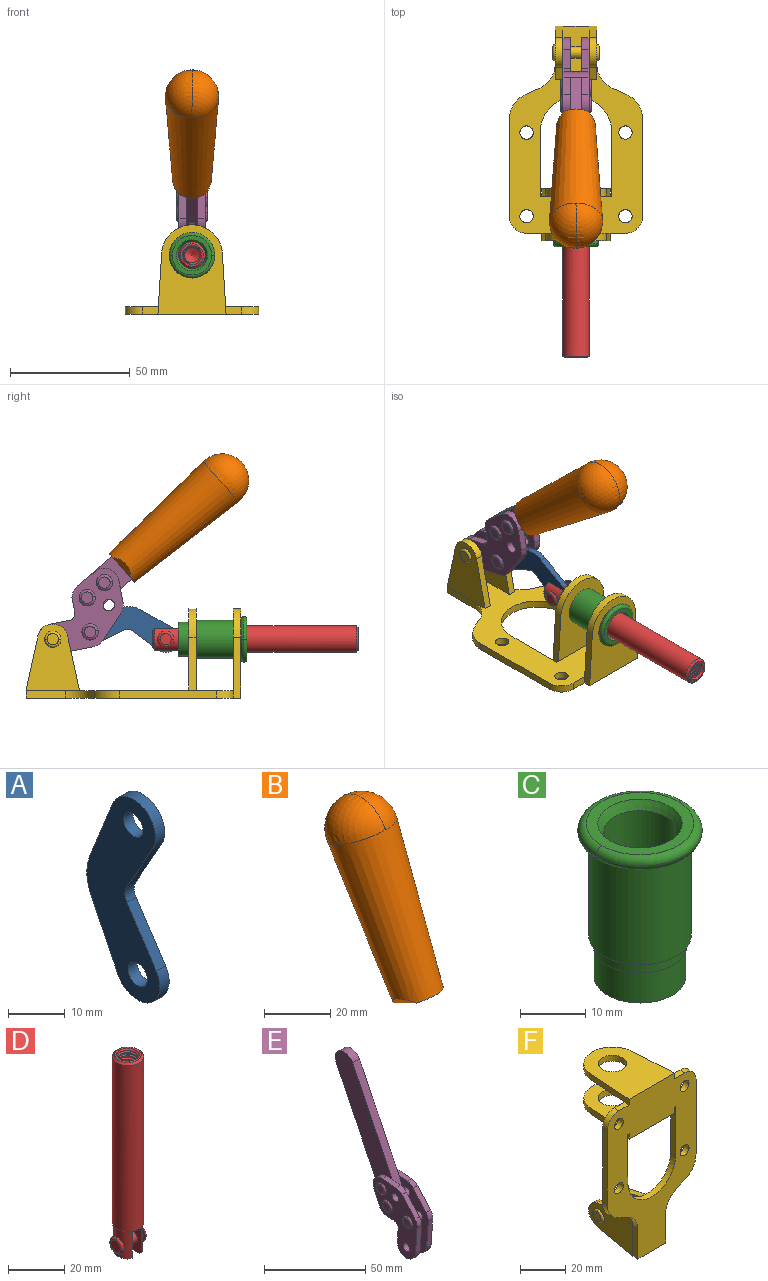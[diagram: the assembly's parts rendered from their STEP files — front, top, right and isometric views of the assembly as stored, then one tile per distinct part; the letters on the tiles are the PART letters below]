
ASSEMBLY  parts=6 mates=6
PART A: 12 faces, bbox 2.3x18.2x42.8 mm
  f0: cylinder r=2.4mm len=4.8mm, axis (1,0,0), area 34.9mm2, adj f4,f11
  f1: cylinder r=10.41mm len=8.47mm, axis (1,0,0), area 20.2mm2, adj f4,f9,f10,f11
  f2: cylinder r=3.05mm len=3.16mm, axis (1,0,0), area 7.7mm2, adj f4,f6,f7,f11
  f3: cylinder r=2.4mm len=4.8mm, axis (1,0,0), area 34.9mm2, adj f4,f11
  f4: plane 42.81x18.23mm, normal (-1,0,0), area 414.1mm2, adj f0,f1,f2,f3,f5,f6,f7,f8
  f5: cylinder r=5.54mm len=10.67mm, axis (1,0,0), area 41.8mm2, adj f4,f6,f10,f11
  f6: plane 11.66x6.53mm, normal (0,-0.87,-0.49), area 30.9mm2, adj f2,f4,f5,f11
  f7: plane 11.17x7.33mm, normal (0,-0.84,0.55), area 30.9mm2, adj f2,f4,f8,f11
  f8: cylinder r=5.54mm len=10.51mm, axis (1,0,0), area 41.8mm2, adj f4,f7,f9,f11
  f9: plane 13.67x6.67mm, normal (0,0.9,-0.44), area 35.1mm2, adj f1,f4,f8,f11
  f10: plane 14.1x5.7mm, normal (0,0.93,0.37), area 35.1mm2, adj f1,f4,f5,f11
  f11: plane 42.81x18.23mm, normal (1,0,0), area 414.1mm2, adj f0,f1,f2,f3,f5,f6,f7,f8
PART B: 11 faces, bbox 22.3x42.6x64.5 mm
  f0: sphere r=11.13mm, area 411.4mm2, adj f1,f8
  f1: cone r=11.11mm half-angle=3.3deg, axis (0,0.44,0.9), area 3251.8mm2, adj f0,f7,f8,f9,f10
  f2: cylinder r=6.16mm len=11.7mm, axis (1,0,0), area 89.5mm2, adj f3,f4,f5,f6
  f3: plane 60.23x36.75mm, normal (-1,0,0), area 763.6mm2, adj f2,f4,f6,f10
  f4: plane 51.37x25.05mm, normal (0,0.9,-0.44), area 264.2mm2, adj f2,f3,f5,f10
  f5: plane 60.23x36.75mm, normal (1,0,0), area 763.6mm2, adj f2,f4,f6,f10
  f6: plane 51.37x25.05mm, normal (0,-0.9,0.44), area 264.2mm2, adj f2,f3,f5,f10
  f7: plane 9.95x5.95mm, normal (0.71,-0.31,-0.64), area 25.8mm2, adj f1,f10
  f8: sphere r=11.13mm, area 411.4mm2, adj f0,f1
  f9: plane 9.95x5.95mm, normal (-0.71,-0.31,-0.64), area 25.8mm2, adj f1,f10
  f10: plane 14.27x11.38mm, normal (0,-0.44,-0.9), area 106.7mm2, adj f1,f3,f4,f5,f6,f7,f9
PART C: 15 faces, bbox 20.6x20.6x28.7 mm
  f0: torus R=8.26mm, axis (0,0,1), area 56.8mm2, adj f1,f10,f12
  f1: torus R=8.26mm, axis (0,0,1), area 56.8mm2, adj f0,f6,f13
  f2: cylinder r=5.59mm len=25.91mm, axis (0,0,1), area 909.6mm2, adj f3,f4
  f3: cone r=6.86mm half-angle=45deg, axis (0,0,-1), area 70.2mm2, adj f2,f14
  f4: cone r=6.47mm half-angle=30deg, axis (0,0,1), area 66.7mm2, adj f2,f13
  f5: cylinder r=7.04mm len=14.07mm, axis (0,0,1), area 252.6mm2, adj f11,f14
  f6: torus R=8.26mm, axis (0,0,1), area 56.8mm2, adj f1,f12,f13
  f7: cylinder r=7.16mm len=14.33mm, axis (0,0,1), area 91.5mm2, adj f9,f11
  f8: cylinder r=7.86mm len=18.42mm, axis (0,0,1), area 909.6mm2, adj f9,f10
  f9: plane 15.72x15.72mm, normal (0,0,-1), area 33mm2, adj f7,f8
  f10: plane 16.51x16.51mm, normal (0,0,-1), area 19.9mm2, adj f0,f8,f12
  f11: plane 14.33x14.33mm, normal (0,0,-1), area 5.7mm2, adj f5,f7
  f12: torus R=8.26mm, axis (0,0,1), area 56.8mm2, adj f0,f6,f10
  f13: plane 16.51x16.51mm, normal (0,0,1), area 82.7mm2, adj f1,f4,f6
  f14: plane 14.07x14.07mm, normal (0,0,-1), area 7.8mm2, adj f3,f5
PART D: 48 faces, bbox 12.6x11.1x86.1 mm
  f0: torus R=2.41mm, axis (-1,0,0), area 15mm2, adj f30,f32,f34
  f1: torus R=2.41mm, axis (-1,0,0), area 15mm2, adj f29,f31,f33
  f2: cylinder r=5.54mm len=72.39mm, axis (0,0,1), area 2518.5mm2, adj f3,f4,f42,f43
  f3: cone r=5.54mm half-angle=45deg, axis (0,0,1), area 7.6mm2, adj f2,f5,f41
  f4: cone r=5.54mm half-angle=45deg, axis (0,0,-1), area 34.9mm2, adj f2,f39
  f5: cylinder r=5.08mm len=11.48mm, axis (0,0,1), area 108.3mm2, adj f3,f7,f8,f41
  f6: cylinder r=2.41mm len=4.83mm, axis (-1,0,0), area 71.2mm2, adj f40,f41
  f7: cylinder r=2.41mm len=4.83mm, axis (-1,0,0), area 7.6mm2, adj f5,f34
  f8: cone r=5.08mm half-angle=45deg, axis (0,0,1), area 10.6mm2, adj f5,f37,f41
  f9: cone r=3.98mm half-angle=45deg, axis (0,0,1), area 17.6mm2, adj f27,f39,f45,f46,f47
  f10: cylinder r=2.41mm len=4.83mm, axis (-1,0,0), area 7.6mm2, adj f33,f38
  f11: cylinder r=3.2mm len=6.4mm, axis (0,0,1), area 78.4mm2, adj f12,f28,f44,f45,f47
  f12: cylinder r=3.2mm len=6.4mm, axis (0,0,1), area 10.5mm2, adj f11,f13,f45,f47
  f13: cylinder r=3.2mm len=6.4mm, axis (0,0,1), area 10.5mm2, adj f12,f14,f45,f47
  f14: cylinder r=3.2mm len=6.4mm, axis (0,0,1), area 10.5mm2, adj f13,f15,f45,f47
  f15: cylinder r=3.2mm len=6.4mm, axis (0,0,1), area 10.5mm2, adj f14,f16,f45,f47
  f16: cylinder r=3.2mm len=6.4mm, axis (0,0,1), area 10.5mm2, adj f15,f17,f45,f47
  f17: cylinder r=3.2mm len=6.4mm, axis (0,0,1), area 10.5mm2, adj f16,f18,f45,f47
  f18: cylinder r=3.2mm len=6.4mm, axis (0,0,1), area 10.5mm2, adj f17,f19,f45,f47
  f19: cylinder r=3.2mm len=6.4mm, axis (0,0,1), area 10.5mm2, adj f18,f20,f45,f47
  f20: cylinder r=3.2mm len=6.4mm, axis (0,0,1), area 10.5mm2, adj f19,f21,f45,f47
  f21: cylinder r=3.2mm len=6.4mm, axis (0,0,1), area 10.5mm2, adj f20,f22,f45,f47
  f22: cylinder r=3.2mm len=6.4mm, axis (0,0,1), area 10.5mm2, adj f21,f23,f45,f47
  f23: cylinder r=3.2mm len=6.4mm, axis (0,0,1), area 10.5mm2, adj f22,f24,f45,f47
  f24: cylinder r=3.2mm len=6.4mm, axis (0,0,1), area 10.5mm2, adj f23,f25,f45,f47
  f25: cylinder r=3.2mm len=6.4mm, axis (0,0,1), area 10.5mm2, adj f24,f26,f45,f47
  f26: cylinder r=3.2mm len=6.4mm, axis (0,0,1), area 10.5mm2, adj f25,f27,f45,f47
  f27: cylinder r=3.2mm len=6.4mm, axis (0,0,1), area 7.4mm2, adj f9,f26,f45,f47
  f28: cone r=3.2mm half-angle=60deg, axis (0,0,1), area 37.2mm2, adj f11
  f29: plane 4.83x4.83mm, normal (-1,0,0), area 18.3mm2, adj f1,f31
  f30: plane 4.83x4.83mm, normal (1,0,0), area 18.3mm2, adj f0,f32
  f31: torus R=2.41mm, axis (-1,0,0), area 15mm2, adj f1,f29,f33
  f32: torus R=2.41mm, axis (-1,0,0), area 15mm2, adj f0,f30,f34
  f33: plane 6.83x6.83mm, normal (1,0,0), area 18.3mm2, adj f1,f10,f31
  f34: plane 6.83x6.83mm, normal (-1,0,0), area 18.3mm2, adj f0,f7,f32
  f35: cone r=5.08mm half-angle=45deg, axis (0,0,1), area 10.6mm2, adj f36,f38,f40
  f36: plane 7.25x1.97mm, normal (0,0,-1), area 10mm2, adj f35,f40
  f37: plane 7.25x1.97mm, normal (0,0,-1), area 10mm2, adj f8,f41
  f38: cylinder r=5.08mm len=11.48mm, axis (0,0,1), area 108.3mm2, adj f10,f35,f40,f42
  f39: plane 9.55x9.55mm, normal (0,0,1), area 22mm2, adj f4,f9
  f40: plane 12.76x10.09mm, normal (1,0,0), area 95.7mm2, adj f6,f35,f36,f38,f42,f43
  f41: plane 12.76x10.09mm, normal (-1,0,0), area 95.7mm2, adj f3,f5,f6,f8,f37,f43
  f42: cone r=5.54mm half-angle=45deg, axis (0,0,1), area 7.6mm2, adj f2,f38,f40
  f43: plane 11.07x4.7mm, normal (0,0,-1), area 50.4mm2, adj f2,f40,f41
  f44: plane 0.89x0.62mm, normal (-1,0,0), area 0.3mm2, adj f11,f45,f46,f47
  f45: bspline ~24.8x7.63mm, area 266.6mm2, adj f9,f11,f12,f13,f14,f15,f16,f17
  f46: bspline ~24.87x7.63mm, area 73.6mm2, adj f9,f44,f45,f47
  f47: bspline ~24.98x7.63mm, area 272.5mm2, adj f9,f11,f12,f13,f14,f15,f16,f17
PART E: 59 faces, bbox 12.9x60.2x99.6 mm
  f0: torus R=2.39mm, axis (-1,0,0), area 14.9mm2, adj f20,f43,f51
  f1: torus R=2.39mm, axis (-1,0,0), area 14.9mm2, adj f19,f42,f51
  f2: torus R=2.39mm, axis (-1,0,0), area 14.9mm2, adj f18,f35,f51
  f3: torus R=2.39mm, axis (-1,0,0), area 14.9mm2, adj f14,f17,f23
  f4: torus R=2.39mm, axis (-1,0,0), area 14.9mm2, adj f13,f16,f23
  f5: torus R=2.39mm, axis (-1,0,0), area 14.9mm2, adj f12,f15,f23
  f6: cylinder r=2.39mm len=4.78mm, axis (1,0,0), area 46.5mm2, adj f48,f50,f51
  f7: cylinder r=2.39mm len=4.78mm, axis (1,0,0), area 46.5mm2, adj f50,f51
  f8: cylinder r=6.35mm len=12.68mm, axis (1,0,0), area 61.8mm2, adj f38,f39,f50,f51
  f9: cylinder r=2.39mm len=4.78mm, axis (-1,0,0), area 70.5mm2, adj f46,f50
  f10: cylinder r=2.39mm len=4.78mm, axis (-1,0,0), area 46.5mm2, adj f23,f45,f46
  f11: cylinder r=2.39mm len=4.78mm, axis (-1,0,0), area 46.5mm2, adj f23,f46
  f12: plane 4.78x4.78mm, normal (1,0,0), area 17.9mm2, adj f5,f15
  f13: plane 4.78x4.78mm, normal (1,0,0), area 17.9mm2, adj f4,f16
  f14: plane 4.78x4.78mm, normal (1,0,0), area 17.9mm2, adj f3,f17
  f15: torus R=2.39mm, axis (-1,0,0), area 14.9mm2, adj f5,f12,f23
  f16: torus R=2.39mm, axis (-1,0,0), area 14.9mm2, adj f4,f13,f23
  f17: torus R=2.39mm, axis (-1,0,0), area 14.9mm2, adj f3,f14,f23
  f18: plane 4.78x4.78mm, normal (-1,0,0), area 17.9mm2, adj f2,f35
  f19: plane 4.78x4.78mm, normal (-1,0,0), area 17.9mm2, adj f1,f42
  f20: plane 4.78x4.78mm, normal (-1,0,0), area 17.9mm2, adj f0,f43
  f21: plane 2.26x0.2mm, normal (1,0,0), area 0.2mm2, adj f31,f44
  f22: plane 2.26x0.2mm, normal (-1,0,0), area 0.2mm2, adj f41,f44
  f23: plane 39.37x30.77mm, normal (1,0,0), area 565.5mm2, adj f3,f4,f5,f10,f11,f15,f16,f17
  f24: cylinder r=6.1mm len=4.15mm, axis (-1,0,0), area 14.7mm2, adj f23,f25,f32,f46
  f25: plane 10.25x9.01mm, normal (0,-0.75,0.66), area 42.3mm2, adj f23,f24,f26,f46
  f26: cylinder r=6.35mm len=4.64mm, axis (-1,0,0), area 15.6mm2, adj f23,f25,f27,f46
  f27: plane 15.84x3.1mm, normal (0,-1,-0.07), area 49.2mm2, adj f23,f26,f28,f46
  f28: cylinder r=6.35mm len=12.68mm, axis (-1,0,0), area 61.8mm2, adj f23,f27,f29,f46
  f29: plane 8.11x3.1mm, normal (0,1,0.07), area 25.2mm2, adj f23,f28,f30,f46
  f30: cylinder r=3.05mm len=3.25mm, axis (-1,0,0), area 14.8mm2, adj f23,f29,f31,f46
  f31: plane 5.99x3.1mm, normal (0,0.07,-1), area 18.6mm2, adj f21,f23,f30,f44,f46
  f32: plane 9.5x3.1mm, normal (0,-0.07,1), area 29.5mm2, adj f23,f24,f33,f46,f47
  f33: cylinder r=6.1mm len=8.63mm, axis (-1,0,0), area 39.1mm2, adj f23,f32,f34,f47
  f34: plane 8.65x3.96mm, normal (0,0.91,-0.42), area 29.5mm2, adj f23,f33,f44,f47
  f35: torus R=2.39mm, axis (-1,0,0), area 14.9mm2, adj f2,f18,f51
  f36: plane 10.25x9.01mm, normal (0,-0.75,0.66), area 42.3mm2, adj f37,f49,f50,f51
  f37: cylinder r=6.35mm len=4.64mm, axis (1,0,0), area 15.6mm2, adj f36,f38,f50,f51
  f38: plane 15.84x3.1mm, normal (0,-1,-0.07), area 49.2mm2, adj f8,f37,f50,f51
  f39: plane 8.11x3.1mm, normal (0,1,0.07), area 25.2mm2, adj f8,f40,f50,f51
  f40: cylinder r=3.05mm len=3.25mm, axis (1,0,0), area 14.8mm2, adj f39,f41,f50,f51
  f41: plane 5.99x3.1mm, normal (0,0.07,-1), area 18.6mm2, adj f22,f40,f44,f50,f51
  f42: torus R=2.39mm, axis (-1,0,0), area 14.9mm2, adj f1,f19,f51
  f43: torus R=2.39mm, axis (-1,0,0), area 14.9mm2, adj f0,f20,f51
  f44: cylinder r=6.35mm len=12.12mm, axis (-1,0,0), area 128.9mm2, adj f21,f22,f23,f31,f34,f41,f46,f47
  f45: plane 2.65x1.35mm, normal (1,0,0), area 1mm2, adj f10,f55
  f46: plane 39.08x20.42mm, normal (-1,0,0), area 412.5mm2, adj f9,f10,f11,f24,f25,f26,f27,f28
  f47: plane 77.62x39.82mm, normal (1,0,0), area 850mm2, adj f32,f33,f34,f44,f53,f54,f55
  f48: plane 2.65x1.35mm, normal (-1,0,0), area 1mm2, adj f6,f55
  f49: cylinder r=6.1mm len=4.15mm, axis (1,0,0), area 14.7mm2, adj f36,f50,f51,f56
  f50: plane 39.08x20.42mm, normal (1,0,0), area 412.5mm2, adj f6,f7,f8,f9,f36,f37,f38,f39
  f51: plane 39.37x30.77mm, normal (-1,0,0), area 565.5mm2, adj f0,f1,f2,f6,f7,f8,f35,f36
  f52: plane 8.65x3.96mm, normal (0,0.91,-0.42), area 29.5mm2, adj f44,f51,f57,f58
  f53: plane 68.49x33.4mm, normal (0,0.9,-0.44), area 358.1mm2, adj f44,f47,f54,f58
  f54: cylinder r=6.35mm len=12.06mm, axis (1,0,0), area 93.7mm2, adj f47,f53,f55,f58
  f55: plane 68.49x33.4mm, normal (0,-0.9,0.44), area 358.1mm2, adj f44,f45,f46,f47,f48,f50,f54,f58
  f56: plane 9.5x3.1mm, normal (0,-0.07,1), area 29.5mm2, adj f49,f50,f51,f57,f58
  f57: cylinder r=6.1mm len=8.63mm, axis (1,0,0), area 39.1mm2, adj f51,f52,f56,f58
  f58: plane 77.62x39.82mm, normal (-1,0,0), area 850mm2, adj f44,f52,f53,f54,f55,f56,f57
PART F: 55 faces, bbox 55.7x37.4x89.8 mm
  f0: torus R=2.41mm, axis (-1,0,0), area 15mm2, adj f11,f15,f25
  f1: torus R=2.41mm, axis (-1,0,0), area 15mm2, adj f10,f12,f22
  f2: cylinder r=2.78mm len=5.56mm, axis (0,-1,0), area 54.2mm2, adj f30,f54
  f3: cylinder r=14.99mm len=29.97mm, axis (0,-1,0), area 145.9mm2, adj f30,f49,f53,f54
  f4: cylinder r=2.78mm len=5.56mm, axis (0,-1,0), area 54.2mm2, adj f30,f54
  f5: cylinder r=2.78mm len=5.56mm, axis (0,-1,0), area 54.2mm2, adj f30,f54
  f6: cylinder r=2.78mm len=5.56mm, axis (0,-1,0), area 54.2mm2, adj f30,f54
  f7: cylinder r=6.35mm len=12.7mm, axis (0,0,1), area 123.6mm2, adj f27,f51
  f8: cylinder r=6.35mm len=12.7mm, axis (0,0,-1), area 124.7mm2, adj f21,f35
  f9: cylinder r=2.41mm len=11.18mm, axis (-1,0,0), area 169.4mm2, adj f16,f19
  f10: plane 4.83x4.83mm, normal (1,0,0), area 18.3mm2, adj f1,f12
  f11: plane 4.83x4.83mm, normal (-1,0,0), area 18.3mm2, adj f0,f15
  f12: torus R=2.41mm, axis (-1,0,0), area 15mm2, adj f1,f10,f22
  f13: cylinder r=6.35mm len=12.41mm, axis (1,0,0), area 53.4mm2, adj f18,f19,f22,f23
  f14: cylinder r=6.35mm len=12.41mm, axis (-1,0,0), area 53.4mm2, adj f16,f17,f24,f25
  f15: torus R=2.41mm, axis (-1,0,0), area 15mm2, adj f0,f11,f25
  f16: plane 27.86x22.35mm, normal (1,0,0), area 425.4mm2, adj f9,f14,f17,f24,f30
  f17: plane 22.86x4.97mm, normal (0,0.21,0.98), area 72.5mm2, adj f14,f16,f25,f30
  f18: plane 22.86x4.97mm, normal (0,0.21,0.98), area 72.5mm2, adj f13,f19,f22,f30
  f19: plane 27.86x22.35mm, normal (-1,0,0), area 425.4mm2, adj f9,f13,f18,f23,f30
  f20: cylinder r=12.7mm len=25.35mm, axis (0,0,-1), area 119.8mm2, adj f21,f34,f35,f36
  f21: plane 34.21x28.07mm, normal (0,0,-1), area 702.4mm2, adj f8,f20,f30,f34,f36
  f22: plane 27.96x22.45mm, normal (1,0,0), area 407.2mm2, adj f1,f12,f13,f18,f23,f30,f42,f43
  f23: plane 22.86x4.97mm, normal (0,0.21,-0.98), area 72.5mm2, adj f13,f19,f22,f44
  f24: plane 22.86x4.97mm, normal (0,0.21,-0.98), area 72.5mm2, adj f14,f16,f25,f44
  f25: plane 27.86x22.35mm, normal (-1,0,0), area 407.1mm2, adj f0,f14,f15,f17,f24,f30,f45,f46
  f26: plane 3.1x0.95mm, normal (0,0,-1), area 2.7mm2, adj f30,f49,f50,f54
  f27: plane 34.21x28.07mm, normal (0,0,1), area 702.4mm2, adj f7,f28,f30,f50,f52
  f28: cylinder r=12.7mm len=25.35mm, axis (0,0,1), area 118.8mm2, adj f27,f50,f51,f52
  f29: plane 3.1x0.95mm, normal (0,0,-1), area 2.7mm2, adj f30,f52,f53,f54
  f30: plane 86.54x55.63mm, normal (0,1,0), area 2362.9mm2, adj f2,f3,f4,f5,f6,f16,f17,f18
  f31: plane 40.56x3.1mm, normal (-1,0,0), area 125.7mm2, adj f30,f32,f48,f54
  f32: cylinder r=7.11mm len=7.11mm, axis (0,-1,0), area 34.6mm2, adj f30,f31,f33,f54
  f33: plane 6.67x3.1mm, normal (0,0,1), area 20.4mm2, adj f30,f32,f34,f54
  f34: plane 25.39x3.13mm, normal (-1,0.06,0), area 79.5mm2, adj f20,f21,f33,f35,f54
  f35: plane 37.31x28.45mm, normal (0,0,1), area 789.9mm2, adj f8,f20,f34,f36,f54
  f36: plane 25.39x3.13mm, normal (1,0.06,0), area 79.5mm2, adj f20,f21,f35,f37,f54
  f37: plane 6.67x3.1mm, normal (0,0,1), area 20.4mm2, adj f30,f36,f38,f54
  f38: cylinder r=7.11mm len=7.11mm, axis (0,-1,0), area 34.6mm2, adj f30,f37,f39,f54
  f39: plane 40.56x3.1mm, normal (1,0,0), area 125.7mm2, adj f30,f38,f40,f54
  f40: cylinder r=11.18mm len=10.16mm, axis (0,-1,0), area 39.5mm2, adj f30,f39,f41,f54
  f41: plane 6.09x3.1mm, normal (0.42,0,-0.91), area 20.8mm2, adj f30,f40,f42,f54
  f42: cylinder r=11.18mm len=9.41mm, axis (0,-1,0), area 37.2mm2, adj f22,f30,f41,f43,f54
  f43: plane 16.5x3.1mm, normal (1,0,0), area 51.1mm2, adj f22,f42,f44,f54
  f44: plane 17.37x3.1mm, normal (0,0,-1), area 53.8mm2, adj f23,f24,f30,f43,f45,f54
  f45: plane 16.5x3.1mm, normal (-1,0,0), area 51.1mm2, adj f25,f44,f46,f54
  f46: cylinder r=11.18mm len=9.41mm, axis (0,-1,0), area 37.2mm2, adj f25,f30,f45,f47,f54
  f47: plane 6.09x3.1mm, normal (-0.42,0,-0.91), area 20.8mm2, adj f30,f46,f48,f54
  f48: cylinder r=11.18mm len=10.16mm, axis (0,-1,0), area 39.5mm2, adj f30,f31,f47,f54
  f49: plane 26.54x3.1mm, normal (-1,0,0), area 82.3mm2, adj f3,f26,f30,f54
  f50: plane 25.39x3.1mm, normal (1,0.06,0), area 78.8mm2, adj f26,f27,f28,f51,f54
  f51: plane 37.31x28.45mm, normal (0,0,-1), area 789.9mm2, adj f7,f28,f50,f52,f54
  f52: plane 25.39x3.1mm, normal (-1,0.06,0), area 78.8mm2, adj f27,f28,f29,f51,f54
  f53: plane 26.54x3.1mm, normal (1,0,0), area 82.3mm2, adj f3,f29,f30,f54
  f54: plane 89.66x55.63mm, normal (0,-1,0), area 2678.5mm2, adj f2,f3,f4,f5,f6,f26,f29,f31
PLACE A rot(axis=(1,0,0),97.5deg) t=(0,12.59,2.22)mm
PLACE B rot(axis=(1,0,0),75deg) t=(0,3.86,9.14)mm
PLACE C rot(axis=(1,0,0),90deg) t=(0,9.14,0)mm
PLACE D rot(axis=(1,0,0),90deg) t=(0,9.52,0)mm
PLACE E rot(axis=(1,0,0),75deg) t=(0,3.86,9.14)mm
PLACE F rot(axis=(1,0,0),90deg) t=(0,9.14,0)mm fixed
MATE fastened B.f2 <-> E.f54  axis (1,0,0) through (0,-30.66,91.94)mm
MATE fastened F.f7 <-> C.f2  axis (0,-1,0) through (0,-37.25,24.61)mm
MATE revolute E.f7 <-> F.f0  axis (-1,0,0) through (0,41.23,24.61)mm
MATE slider D.f2 <-> C.f2  axis (0,-1,0) through (0,-49.26,24.61)mm
MATE revolute E.f4 <-> A.f3  axis (-1,0,0) through (0,25.65,27.64)mm
MATE revolute A.f5 <-> D.f6  axis (1,0,0) through (0,-5.96,24.61)mm
